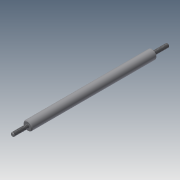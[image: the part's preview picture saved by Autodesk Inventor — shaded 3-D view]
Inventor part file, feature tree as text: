
AUTODESK INVENTOR PART (.ipt)
format: ipt  version: 2013 (Build 170138000, 138)  size: 94,208 bytes
history: native  units: mm
features: sketch x5, extrude x3, chamfer x3, hole x2, thread x2
ambient origin geometry x8: Origin, YZ Plane, XZ Plane, XY Plane, X Axis, Y Axis, Z Axis, Center Point
bodies: Solid1 (feature_tree)
feature tree (15):
  extrude  "Extrusion1"  Depth=82.6mm TaperAngle=0.0deg
  hole  "Hole1"  [1 undecoded]
  hole  "Hole2"  [1 undecoded]
  chamfer  "Chamfer1"  Distance=10.0mm
  extrude  "Extrusion2"  Depth=0.3mm TaperAngle=45.0deg
  extrude  "Extrusion3"  Depth=0.3mm TaperAngle=45.0deg
  thread  "Thread1"  [1 undecoded]
  thread  "Thread2"  [1 undecoded]
  chamfer  "Chamfer2"  [1 undecoded]
  chamfer  "Chamfer3"  [1 undecoded]
  sketch  "Sketch1"  dims[d0=6.0mm d1=82.6mm d2=0.0mm]
  sketch  "Sketch2"  dims[d3=2.459mm d4=6.0mm d5=4.0mm d6=2.0mm d7=90.0deg d8=8.0mm d9=0.0mm]
  sketch  "Sketch3"  dims[d10=2.459mm d11=6.0mm d12=4.0mm d13=2.0mm d14=90.0deg d15=8.0mm d16=0.0mm d17=0.5mm d18=2.0mm d19=45.0deg]
  sketch  "Sketch4"  dims[d20=10.0mm d21=0.0mm d22=10.0mm d23=0.0mm d24=10.0mm d25=0.0mm]
  sketch  "Sketch5"  dims[d26=10.0mm d27=0.0mm d28=0.3mm d29=2.0mm d30=45.0deg d31=0.3mm d32=2.0mm d33=45.0deg]
note: 6 required parameter values undecoded (feature->parameter linkage not recoverable at this tier; creation-order binding heuristic only, values carry confidence <= 0.55)
